# Revit family: 6295-6298_Enclosed Conventional Heat Detector
name_source: partatom
category: Fire Alarm Devices
units: mm (PartAtom-declared; Revit-internal decimal feet)

## family parameters
Cut with Voids When Loaded = No
Host = Face
Maintain Annotation Orientation = No
OmniClass Number = 23.85.30.21
OmniClass Title = Environmental Detection/Registration
Part Type = Normal
Room Calculation Point = No
Round Connector Dimension = Use Diameter
Shared = No

## types (4) — shared parameters
Ambient Humidity = Maximum 95 % RH
Ambient Temperature Storage = -45 to +70 °C
Clearance Area = Clearance Area
Current Quiescent = 0 mA
Height (mm) = 75 mm
Ingress Protection Rating = IP67
Manufacturer = Panasonic
Max_Wire Size = Ø 1.2 mm (1.13 mm²)
Min_Wire Size = Ø 0.6 mm (0.3 mm²)
Omniclass Code = 23.85.30.21.11.11.11
Omniclass Description = Smoke Detectors
Product Material = Polycarbonate_Panasonic_Grey
Tested and Approved = EN54-5
URL = https://www.panasonic-fire-security.com
Uniclass 2015 Code = Pr_75_80_30_27
Uniclass 2015 Description = Fire and smoke detector bases
Uniformat 2010  Code = D7050
Uniformat 2010 Description = Detection and Alarm
Version = RVT20
Voltage Allowed = 12 – 30 VDC
Voltage Normal = 24 VDC (Zone Line)
Weight = 82g
ø (mm) = 100 mm  [stored 0.328084 ft]
zero-valued in all types: Default Elevation

## per-type parameters (varying)
| type | ATEX Classification | Ambient Temperature Operating | CPR | Current (Active) | Description | Type Comments |
| 6295 | II 3 G Ex ic IIC T5 Gc X, II 3 D Ex ic IIIC T100°C Dc X
-40°C ? Ta ? 50°C / EN IEC 60079-0:2018, 
EN 60079-11:2012 | -40 to +50 °C | 2531-CPR-232.1192 | 35 mA | Enclosed conventional heat detector 6295 | 6295 is a conventional fixed temperature heat detector. The detector will give an alarm at a certain fixed temperature (57 °C). The detector is intended for outdoor use or indoor use in high humidity premises |
| 6296 | II 3 G Ex ic IIC T5 Gc X, II 3 D Ex ic IIIC T100°C Dc X
-40°C ? Ta ? 50°C / EN IEC 60079-0:2018, 
EN 60079-11:2012 | -40 to +65 °C | 2531-CPR-232.1193 | 35 mA | Enclosed conventional heat detector 6296 | 6296 is a conventional fixed temperature heat detector. The detector will give an alarm at a certain fixed temperature (72 °C). The detector is intended for outdoor use or indoor use in high humidity premises |
| 6297 | - | -40 to +80 °C | 2531-CPR-232.1194 | 35 mA | Enclosed conventional heat detector 6297 | 6297 is a conventional fixed temperature heat detector. The detector will give an alarm at a certain fixed temperature (87 °C). The detector is intended for outdoor use or indoor use in high humidity premises |
| 6298 | - | -40 to +110 °C | 2531-CPR-232.1195 | 25 mA | Enclosed conventional heat detector 6298 | 6298 is a conventional fixed temperature heat detector. The detector will give an alarm at a certain fixed temperature (117 °C). The detector is intended for outdoor use or indoor use in high humidity premises |

note: column(s) folded — value = type name in every type: Model

note: [stored X ft] marks values corroborated as IEEE doubles in the binary element streams (Revit-internal decimal feet)

## geometry (parser evidence)
native form markers: Sweep x2
no freeform markers — native parametric forms only
